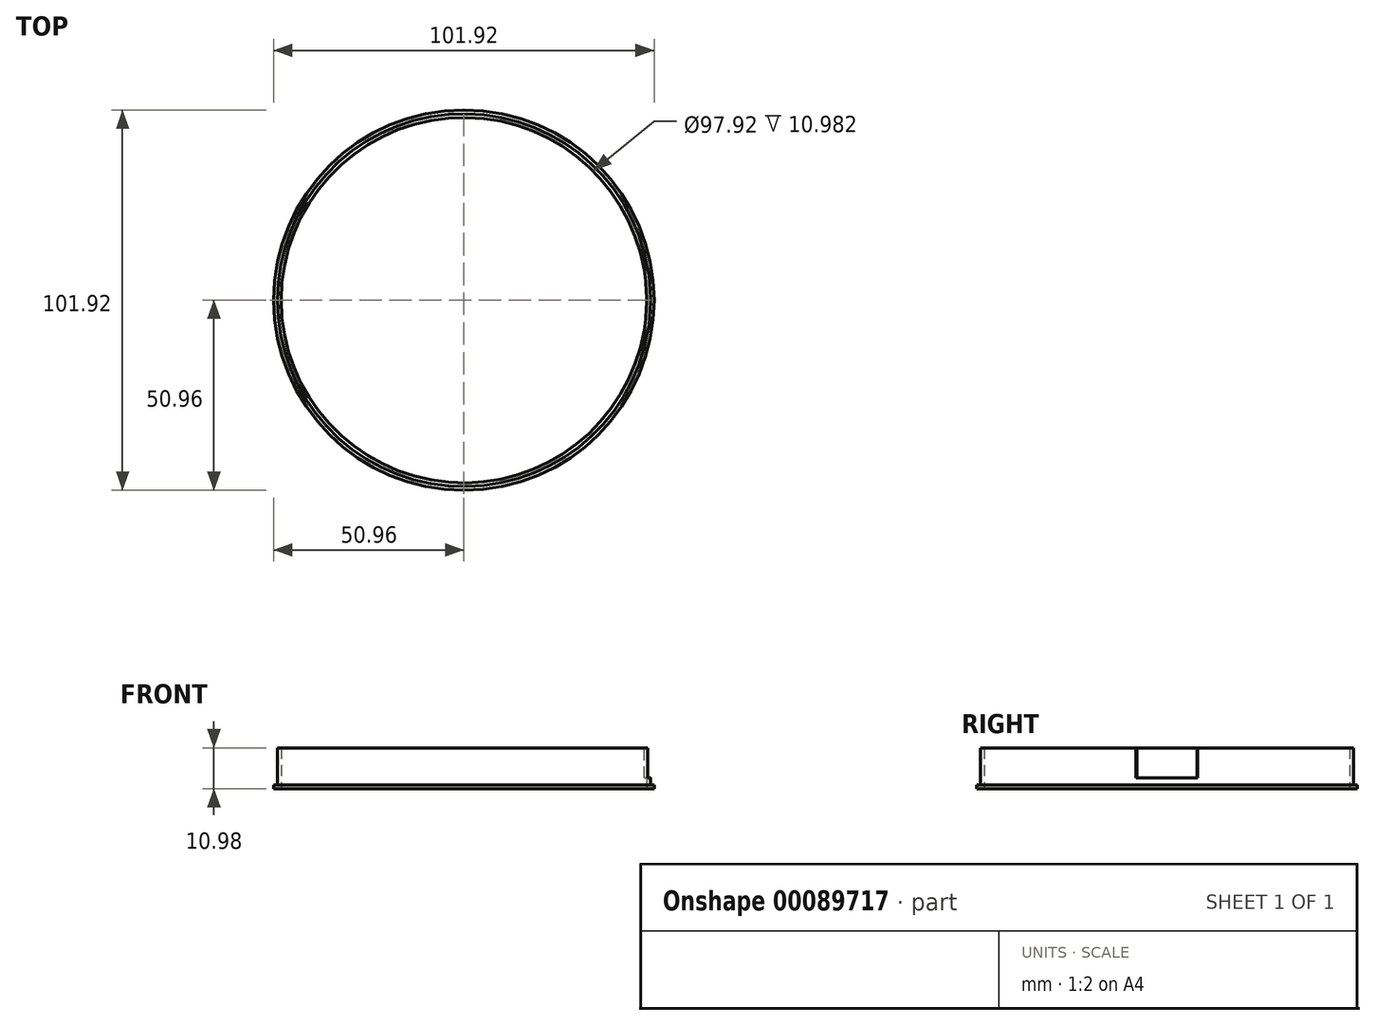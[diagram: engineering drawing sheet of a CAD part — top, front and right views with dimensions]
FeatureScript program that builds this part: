
annotation { "Feature Type Name" : "Feature", "Feature Type Description" : "" }
export const myFeature = defineFeature(function(context is Context, id is Id, definition is map)
    precondition{}
    {
        {
            var Q0;
            Q0=qCreatedBy(makeId("Front.planeOp"),FACE);
            var sketch = newSketch(context, id + "F0", { "sketchPlane" : qUnion([Q0])});
            skLineSegment(sketch, "E0", {"start": v(48.96, 0) * mm, "end": v(48.96, 11) * mm});
            skLineSegment(sketch, "E1", {"start": v(48.96, 11) * mm, "end": v(49.96, 11) * mm});
            skLineSegment(sketch, "E2", {"start": v(49.96, 11) * mm, "end": v(49.96, 1) * mm});
            skLineSegment(sketch, "E3", {"start": v(49.96, 1) * mm, "end": v(50.96, 1) * mm});
            skLineSegment(sketch, "E4", {"start": v(50.96, 1) * mm, "end": v(50.96, 0) * mm});
            skLineSegment(sketch, "E5", {"start": v(50.96, 0) * mm, "end": v(48.96, 0) * mm});
            skPoint(sketch, "E6", {"position": v(0, 0) * mm});
            skLineSegment(sketch, "E7", {"start": v(0, 0) * mm, "end": v(0, 17.76) * mm});
            skLineSegment(sketch, "E8.bottom", {"start": v(49.96, 10.98) * mm, "end": v(48.96, 10.98) * mm});
            skLineSegment(sketch, "E8.top", {"start": v(49.96, 2.98) * mm, "end": v(48.96, 2.98) * mm});
            skLineSegment(sketch, "E8.left", {"start": v(49.96, 10.98) * mm, "end": v(49.96, 2.98) * mm});
            skLineSegment(sketch, "E8.right", {"start": v(48.96, 10.98) * mm, "end": v(48.96, 2.98) * mm});
            skPoint(sketch, "E8.middle", {"position": v(49.46, 6.98) * mm});
            skSolve(sketch);
        }
        {
            var Q0;
            {var subQ0=sQuery(id+"F0.wireOp",EDGE,"E3");Q0=makeQuery(id+"F0.imprint","IMPRINT",FACE,{"disambiguationData":[TD([[makeQuery(id+"F0.imprint","IMPRINT",EDGE,{"derivedFrom":subQ0}),-1.0]])]});}
            var Q1;
            Q1=makeQuery(id+"F0.imprint","IMPRINT",FACE,{"disambiguationData":[TD([[makeQuery(id+"F0.imprint","IMPRINT",EDGE,{"derivedFrom":sQuery(id+"F0.wireOp",EDGE,"E8.bottom")}),1.0]])]});
            var Q2;
            Q2=sQuery(id+"F0.wireOp",EDGE,"E7");
            revolve(context, id + "F1", {"entities" : qUnion([Q0, Q1]), "axis" : qUnion([Q2]), "revolveType" : RevolveType.FULL});
        }
        {
            var Q0;
            {var subQ5=sQuery(id+"F0.wireOp",EDGE,"E8.left");Q0=makeQuery(id+"F0.imprint","IMPRINT",FACE,{"disambiguationData":[TD([[makeQuery(id+"F0.imprint","IMPRINT",EDGE,{"derivedFrom":subQ5}),-1.0]])]});}
            var Q1;
            {var subQ0=sQuery(id+"F0.wireOp",EDGE,"E8.top");var subQ1=sQuery(id+"F0.wireOp",EDGE,"E0");var subQ2=makeQuery(id+"F0.imprint","INTERSECT",VERTEX,{"derivedFrom":[subQ1,subQ0]});Q1=makeQuery(id+"F0.imprint","IMPRINT",FACE,{"disambiguationData":[TD([[makeQuery(id+"F0.imprint","IMPRINT",EDGE,{"disambiguationData":[TD([[subQ2,-1.0]])],"derivedFrom":subQ1}),-1.0]])]});}
            var Q2;
            Q2=sQuery(id+"F0.wireOp",EDGE,"E7");
            revolve(context, id + "F2", {"operationType" : NewBodyOperationType.REMOVE, "entities" : qUnion([Q0, Q1]), "axis" : qUnion([Q2]), "revolveType" : RevolveType.SYMMETRIC, "angle" : 19 * degree});
        }
    });
